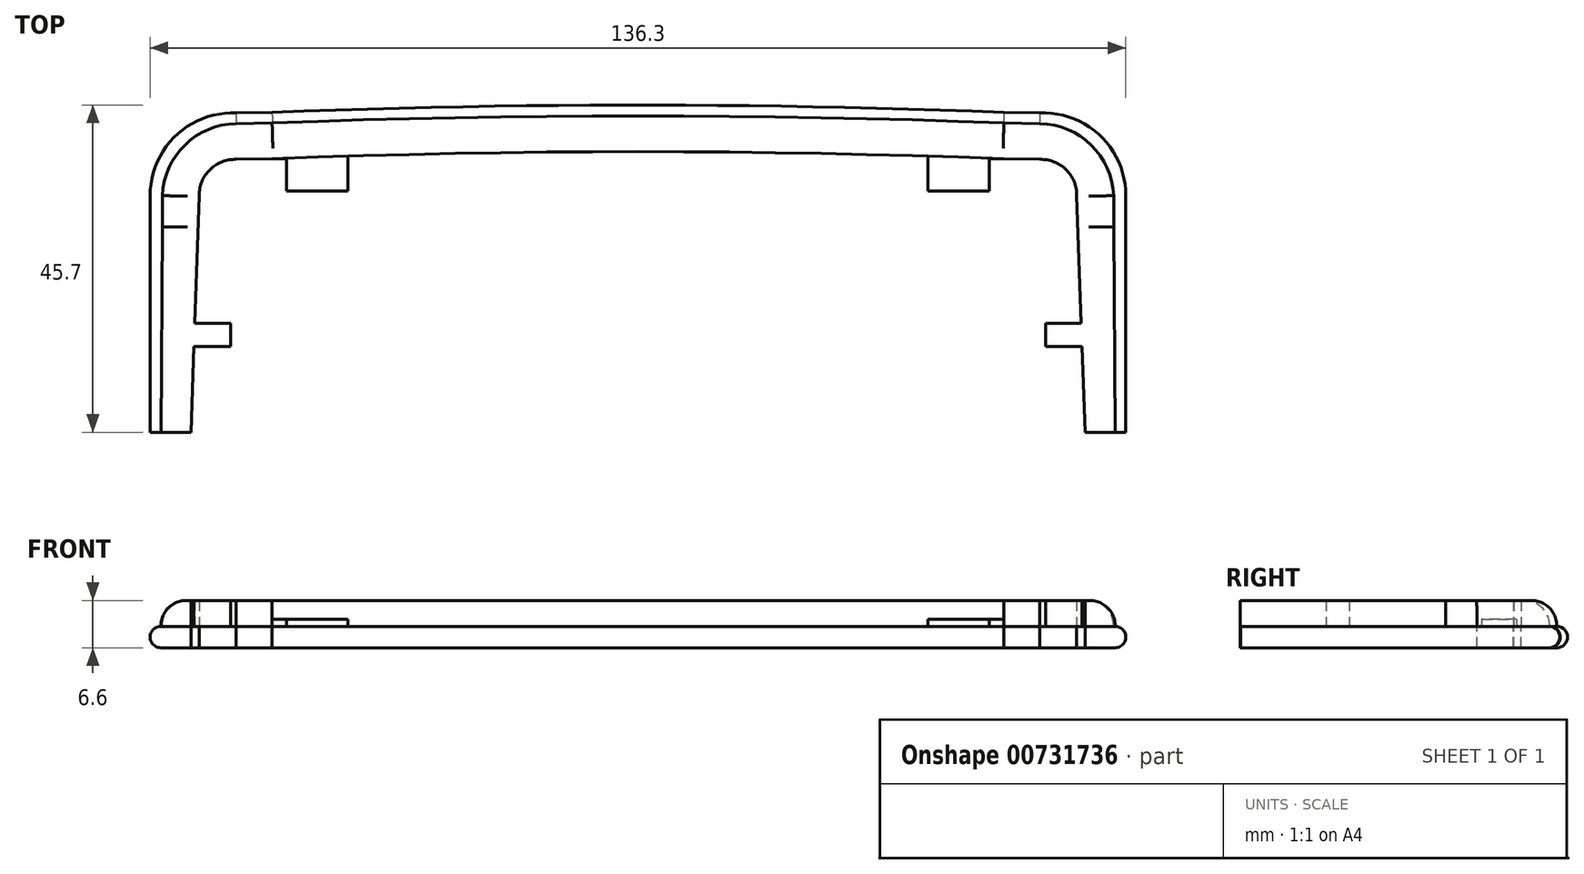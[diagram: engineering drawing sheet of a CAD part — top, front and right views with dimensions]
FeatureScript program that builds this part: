
annotation { "Feature Type Name" : "Feature", "Feature Type Description" : "" }
export const myFeature = defineFeature(function(context is Context, id is Id, definition is map)
    precondition{}
    {
        {
            var Q0;
            Q0=qCreatedBy(makeId("Top.planeOp"),FACE);
            var sketch = newSketch(context, id + "F0", { "sketchPlane" : qUnion([Q0])});
            skLineSegment(sketch, "E0", {"start": v(-40.5, 6.3) * mm, "end": v(40.5, 6.3) * mm, "construction": true});
            skPoint(sketch, "E1", {"position": v(0, 6.3) * mm});
            skPoint(sketch, "E2", {"position": v(-49.1, 6.3) * mm});
            skPoint(sketch, "E3", {"position": v(49.1, 6.3) * mm});
            skPoint(sketch, "E4", {"position": v(0, 6.8) * mm});
            skPoint(sketch, "E5", {"position": v(-49.1, 5.8) * mm});
            skPoint(sketch, "E6", {"position": v(49.1, 5.8) * mm});
            skLineSegment(sketch, "E7", {"start": v(-40.5, 6.3) * mm, "end": v(-40.5, 1.3) * mm});
            skLineSegment(sketch, "E8", {"start": v(-40.5, 1.3) * mm, "end": v(-49.1, 1.3) * mm});
            skLineSegment(sketch, "E9", {"start": v(-49.1, 1.3) * mm, "end": v(-49.1, 5.8) * mm});
            skLineSegment(sketch, "E10", {"start": v(40.5, 6.3) * mm, "end": v(40.5, 1.3) * mm});
            skLineSegment(sketch, "E11", {"start": v(40.5, 1.3) * mm, "end": v(49.1, 1.3) * mm});
            skLineSegment(sketch, "E12", {"start": v(49.1, 1.3) * mm, "end": v(49.1, 5.8) * mm});
            skLineSegment(sketch, "E13", {"start": v(49.1, 6.3) * mm, "end": v(89.1, 6.3) * mm, "construction": true});
            skLineSegment(sketch, "E14", {"start": v(-49.1, 6.3) * mm, "end": v(-89.1, 6.3) * mm, "construction": true});
            skLineSegment(sketch, "E15", {"start": v(61.1, 6.3) * mm, "end": v(63.17, -53.01) * mm, "construction": true});
            skPoint(sketch, "E16", {"position": v(51.11, 5.8) * mm});
            skPoint(sketch, "E17", {"position": v(61.45, -3.7) * mm});
            skLineSegment(sketch, "E18", {"start": v(49.1, 5.8) * mm, "end": v(51.11, 5.8) * mm});
            skPoint(sketch, "E19", {"position": v(61.92, -17.2) * mm});
            skPoint(sketch, "E20", {"position": v(62.03, -20.4) * mm});
            skLineSegment(sketch, "E21", {"start": v(61.92, -17.2) * mm, "end": v(56.92, -17.2) * mm});
            skLineSegment(sketch, "E22", {"start": v(56.92, -17.2) * mm, "end": v(56.92, -20.4) * mm});
            skLineSegment(sketch, "E23", {"start": v(56.92, -20.4) * mm, "end": v(62.03, -20.4) * mm});
            skLineSegment(sketch, "E24", {"start": v(61.45, -3.7) * mm, "end": v(61.92, -17.2) * mm});
            skPoint(sketch, "E25", {"position": v(62.45, -32.4) * mm});
            skLineSegment(sketch, "E26", {"start": v(62.03, -20.4) * mm, "end": v(62.45, -32.4) * mm});
            skPoint(sketch, "E27.MirrorP", {"position": v(-51.11, 5.8) * mm});
            skLineSegment(sketch, "E28.MirrorCS", {"start": v(-61.92, -17.2) * mm, "end": v(-56.92, -17.2) * mm});
            skLineSegment(sketch, "E29.MirrorCS", {"start": v(-56.92, -17.2) * mm, "end": v(-56.92, -20.4) * mm});
            skLineSegment(sketch, "E30.MirrorCS", {"start": v(-56.92, -20.4) * mm, "end": v(-62.03, -20.4) * mm});
            skPoint(sketch, "E31.MirrorP", {"position": v(-62.45, -32.4) * mm});
            skLineSegment(sketch, "E32", {"start": v(-49.1, 5.8) * mm, "end": v(-51.11, 5.8) * mm});
            skLineSegment(sketch, "E33", {"start": v(-61.45, -3.7) * mm, "end": v(-61.92, -17.2) * mm});
            skLineSegment(sketch, "E34", {"start": v(-62.03, -20.4) * mm, "end": v(-62.45, -32.4) * mm});
            skPoint(sketch, "E35", {"position": v(66.65, -32.4) * mm});
            skLineSegment(sketch, "E36", {"start": v(62.45, -32.4) * mm, "end": v(66.65, -32.4) * mm});
            skLineSegment(sketch, "E37.MirrorCS", {"start": v(-62.45, -32.4) * mm, "end": v(-66.65, -32.4) * mm});
            skPoint(sketch, "E38", {"position": v(0, 11.8) * mm});
            skPoint(sketch, "E39", {"position": v(51.11, 10.8) * mm});
            skPoint(sketch, "E40", {"position": v(66.45, -3.7) * mm});
            skPoint(sketch, "E41.MirrorP", {"position": v(-51.11, 10.8) * mm});
            skPoint(sketch, "E42.MirrorP", {"position": v(-66.45, -3.7) * mm});
            skLineSegment(sketch, "E43", {"start": v(-66.65, -32.4) * mm, "end": v(-66.45, -3.7) * mm});
            skLineSegment(sketch, "E44", {"start": v(66.65, -32.4) * mm, "end": v(66.45, -3.7) * mm});
            skArc(sketch, "E45", {"start": v(51.11, 10.8) * mm, "mid": v(0, 11.8) * mm, "end": v(-51.11, 10.8) * mm});
            skLineSegment(sketch, "E46", {"start": v(-61.92, -17.2) * mm, "end": v(-62.03, -20.4) * mm});
            skLineSegment(sketch, "E47", {"start": v(61.92, -17.2) * mm, "end": v(62.03, -20.4) * mm});
            skArc(sketch, "E48", {"start": v(51.11, 5.8) * mm, "mid": v(0, 6.8) * mm, "end": v(-51.11, 5.8) * mm});
            skLineSegment(sketch, "E49", {"start": v(-66.65, -32.4) * mm, "end": v(-68.15, -32.39) * mm});
            skLineSegment(sketch, "E50", {"start": v(-68.15, -32.39) * mm, "end": v(-68.15, -3.7) * mm});
            skPoint(sketch, "E51", {"position": v(-51.11, 12.3) * mm});
            skPoint(sketch, "E52", {"position": v(0, 13.3) * mm});
            skPoint(sketch, "E53", {"position": v(51.11, 12.3) * mm});
            skLineSegment(sketch, "E54.MirrorCS", {"start": v(68.15, -32.39) * mm, "end": v(68.15, -3.7) * mm});
            skLineSegment(sketch, "E55.MirrorCS", {"start": v(66.65, -32.4) * mm, "end": v(68.15, -32.39) * mm});
            skArc(sketch, "E56", {"start": v(51.11, 12.3) * mm, "mid": v(0, 13.3) * mm, "end": v(-51.11, 12.3) * mm});
            skLineSegment(sketch, "E57", {"start": v(49.1, 5.8) * mm, "end": v(70.74, 5.55) * mm, "construction": true});
            skPoint(sketch, "E58", {"position": v(56.12, 5.72) * mm});
            skPoint(sketch, "E59", {"position": v(61.3, 0.66) * mm});
            skArc(sketch, "E60", {"start": v(61.3, 0.66) * mm, "mid": v(59.8, 4.3) * mm, "end": v(56.12, 5.72) * mm});
            skLineSegment(sketch, "E61", {"start": v(51.11, 5.8) * mm, "end": v(56.12, 5.72) * mm});
            skLineSegment(sketch, "E62", {"start": v(61.3, 0.66) * mm, "end": v(61.45, -3.7) * mm});
            skArc(sketch, "E63.MirrorCS", {"start": v(-61.3, 0.66) * mm, "mid": v(-59.8, 4.3) * mm, "end": v(-56.12, 5.72) * mm});
            skLineSegment(sketch, "E64", {"start": v(-56.12, 5.72) * mm, "end": v(-51.11, 5.8) * mm});
            skLineSegment(sketch, "E65", {"start": v(-61.3, 0.66) * mm, "end": v(-61.45, -3.7) * mm});
            skPoint(sketch, "E66", {"position": v(56.12, 10.72) * mm});
            skPoint(sketch, "E67", {"position": v(56.12, 12.22) * mm});
            skPoint(sketch, "E68", {"position": v(66.45, 0.66) * mm});
            skPoint(sketch, "E69", {"position": v(68.15, 0.66) * mm});
            skLineSegment(sketch, "E70", {"start": v(51.11, 10.8) * mm, "end": v(56.12, 10.72) * mm});
            skLineSegment(sketch, "E71", {"start": v(51.11, 12.3) * mm, "end": v(56.12, 12.22) * mm});
            skLineSegment(sketch, "E72", {"start": v(66.45, -3.7) * mm, "end": v(66.45, 0.66) * mm});
            skLineSegment(sketch, "E73", {"start": v(68.15, 0.66) * mm, "end": v(68.15, -3.7) * mm});
            skArc(sketch, "E74", {"start": v(66.45, 0.66) * mm, "mid": v(63.28, 7.74) * mm, "end": v(56.12, 10.72) * mm});
            skArc(sketch, "E75", {"start": v(68.15, 0.66) * mm, "mid": v(64.6, 9) * mm, "end": v(56.12, 12.22) * mm});
            skLineSegment(sketch, "E76.MirrorCS", {"start": v(-68.15, 0.66) * mm, "end": v(-68.15, -3.7) * mm});
            skLineSegment(sketch, "E77.MirrorCS", {"start": v(-66.45, -3.7) * mm, "end": v(-66.45, 0.66) * mm});
            skLineSegment(sketch, "E78.MirrorCS", {"start": v(-51.11, 12.3) * mm, "end": v(-56.12, 12.22) * mm});
            skLineSegment(sketch, "E79.MirrorCS", {"start": v(-51.11, 10.8) * mm, "end": v(-56.12, 10.72) * mm});
            skArc(sketch, "E80.MirrorCS", {"start": v(-68.15, 0.66) * mm, "mid": v(-64.6, 9) * mm, "end": v(-56.12, 12.22) * mm});
            skArc(sketch, "E81.MirrorCS", {"start": v(-66.45, 0.66) * mm, "mid": v(-63.28, 7.74) * mm, "end": v(-56.12, 10.72) * mm});
            skSolve(sketch);
        }
        {
            var Q0;
            Q0=makeQuery(id+"F0.imprint","IMPRINT",FACE,{"disambiguationData":[TD([[makeQuery(id+"F0.imprint","IMPRINT",EDGE,{"derivedFrom":sQuery(id+"F0.wireOp",EDGE,"E7")}),-1.0]])]});
            var Q1;
            {var subQ1=sQuery(id+"F0.wireOp",EDGE,"E11");Q1=makeQuery(id+"F0.imprint","IMPRINT",FACE,{"disambiguationData":[TD([[makeQuery(id+"F0.imprint","IMPRINT",EDGE,{"derivedFrom":subQ1}),1.0]])]});}
            extrude(context, id + "F1", {"entities" : qUnion([Q0, Q1]), "depth" : 1 * mm, "offsetDistance" : 25 * mm});
        }
        {
            var Q0;
            Q0=makeQuery(id+"F0.imprint","IMPRINT",FACE,{"disambiguationData":[TD([[makeQuery(id+"F0.imprint","IMPRINT",EDGE,{"derivedFrom":sQuery(id+"F0.wireOp",EDGE,"E24")}),1.0]])]});
            var Q1;
            Q1=makeQuery(id+"F0.imprint","IMPRINT",FACE,{"disambiguationData":[TD([[makeQuery(id+"F0.imprint","IMPRINT",EDGE,{"derivedFrom":sQuery(id+"F0.wireOp",EDGE,"E28.MirrorCS")}),-1.0]])]});
            var Q2;
            Q2=makeQuery(id+"F0.imprint","IMPRINT",FACE,{"disambiguationData":[TD([[makeQuery(id+"F0.imprint","IMPRINT",EDGE,{"derivedFrom":sQuery(id+"F0.wireOp",EDGE,"E21")}),1.0]])]});
            extrude(context, id + "F2", {"entities" : qUnion([Q0, Q1, Q2]), "operationType" : NewBodyOperationType.ADD, "depth" : 3.6 * mm, "offsetDistance" : 25 * mm});
        }
        {
            var Q0;
            Q0=makeQuery(id+"F2.opExtrude","CAP_EDGE",EDGE,{"disambiguationData":[OSD([sQuery(id+"F0.wireOp",EDGE,"E44")])],"isStart":false});
            var Q1;
            Q1=makeQuery(id+"F2.opExtrude","CAP_EDGE",EDGE,{"disambiguationData":[OSD([sQuery(id+"F0.wireOp",EDGE,"0276d141-66d3-4eb9-91e6-7a26046694350.MirrorCS")])],"isStart":false});
            var Q2;
            Q2=makeQuery(id+"F2.opExtrude","CAP_EDGE",EDGE,{"disambiguationData":[OSD([sQuery(id+"F0.wireOp",EDGE,"E45")])],"isStart":false});
            var Q3;
            Q3=makeQuery(id+"F2.opExtrude","CAP_EDGE",EDGE,{"disambiguationData":[OSD([sQuery(id+"F0.wireOp",EDGE,"nQ1ebCfD-D8iv-tbj2-Of3A-sHUVGAhPEN3i")])],"isStart":false});
            var Q4;
            Q4=makeQuery(id+"F2.opExtrude","CAP_EDGE",EDGE,{"disambiguationData":[OSD([sQuery(id+"F0.wireOp",EDGE,"E43")])],"isStart":false});
            fillet(context, id + "F3", {"entities" : qUnion([Q0, Q1, Q2, Q3, Q4]), "radius" : 3.5 * mm, "tangentPropagation" : true, "allowEdgeOverflow" : false});
        }
        {
            var Q0;
            Q0=makeQuery(id+"F0.imprint","IMPRINT",FACE,{"disambiguationData":[TD([[makeQuery(id+"F0.imprint","IMPRINT",EDGE,{"derivedFrom":sQuery(id+"F0.wireOp",EDGE,"E24")}),1.0]])]});
            var Q1;
            Q1=makeQuery(id+"F0.imprint","IMPRINT",FACE,{"disambiguationData":[TD([[makeQuery(id+"F0.imprint","IMPRINT",EDGE,{"derivedFrom":sQuery(id+"F0.wireOp",EDGE,"E43")}),1.0]])]});
            extrude(context, id + "F4", {"entities" : qUnion([Q0, Q1]), "oppositeDirection" : true, "depth" : 3 * mm, "offsetDistance" : 25 * mm});
        }
        {
            var Q0;
            Q0=makeQuery(id+"F4.opExtrude","CAP_EDGE",EDGE,{"disambiguationData":[OSD([sQuery(id+"F0.wireOp",EDGE,"E50")])],"isStart":true});
            var Q1;
            Q1=makeQuery(id+"F4.opExtrude","CAP_EDGE",EDGE,{"disambiguationData":[OSD([sQuery(id+"F0.wireOp",EDGE,"E56")])],"isStart":true});
            var Q2;
            Q2=makeQuery(id+"F4.opExtrude","CAP_EDGE",EDGE,{"disambiguationData":[OSD([sQuery(id+"F0.wireOp",EDGE,"E54.MirrorCS")])],"isStart":true});
            var Q3;
            Q3=makeQuery(id+"F4.opExtrude","CAP_EDGE",EDGE,{"disambiguationData":[OSD([sQuery(id+"F0.wireOp",EDGE,"E54.MirrorCS")])],"isStart":false});
            var Q4;
            Q4=makeQuery(id+"F4.opExtrude","CAP_EDGE",EDGE,{"disambiguationData":[OSD([sQuery(id+"F0.wireOp",EDGE,"E56")])],"isStart":false});
            var Q5;
            Q5=makeQuery(id+"F4.opExtrude","CAP_EDGE",EDGE,{"disambiguationData":[OSD([sQuery(id+"F0.wireOp",EDGE,"E50")])],"isStart":false});
            fillet(context, id + "F5", {"entities" : qUnion([Q0, Q1, Q2, Q3, Q4, Q5]), "radius" : 1.5 * mm, "tangentPropagation" : true, "allowEdgeOverflow" : false});
        }
    });
